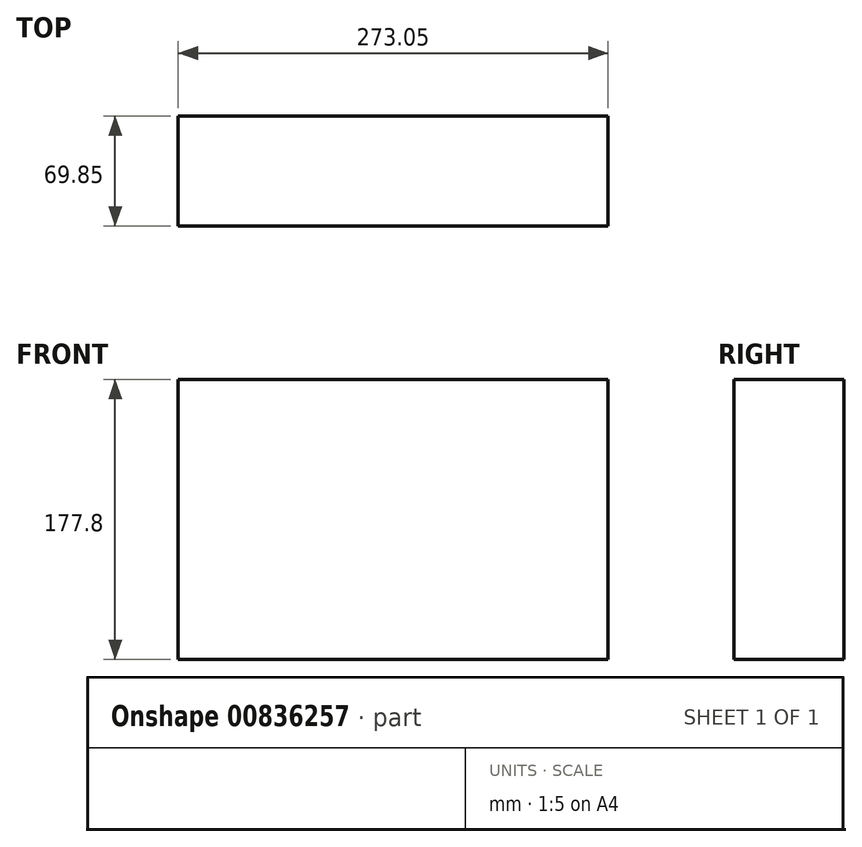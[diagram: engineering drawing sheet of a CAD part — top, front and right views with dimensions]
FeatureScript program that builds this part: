
annotation { "Feature Type Name" : "Feature", "Feature Type Description" : "" }
export const myFeature = defineFeature(function(context is Context, id is Id, definition is map)
    precondition{}
    {
        {
            var Q0;
            Q0=qCreatedBy(makeId("Front.planeOp"),FACE);
            var sketch = newSketch(context, id + "F0", { "sketchPlane" : qUnion([Q0])});
            skLineSegment(sketch, "E0.bottom", {"start": v(0, 0) * mm, "end": v(273.05, 0) * mm});
            skLineSegment(sketch, "E0.top", {"start": v(0, 177.8) * mm, "end": v(273.05, 177.8) * mm});
            skLineSegment(sketch, "E0.left", {"start": v(0, 0) * mm, "end": v(0, 177.8) * mm});
            skLineSegment(sketch, "E0.right", {"start": v(273.05, 0) * mm, "end": v(273.05, 177.8) * mm});
            skSolve(sketch);
        }
        {
            var Q0;
            Q0 = qSketchRegion(id + "F0", true);
            extrude(context, id + "F1", {"entities" : qUnion([Q0]), "oppositeDirection" : true, "depth" : 69.85 * mm, "offsetDistance" : 25.4 * mm});
        }
    });
